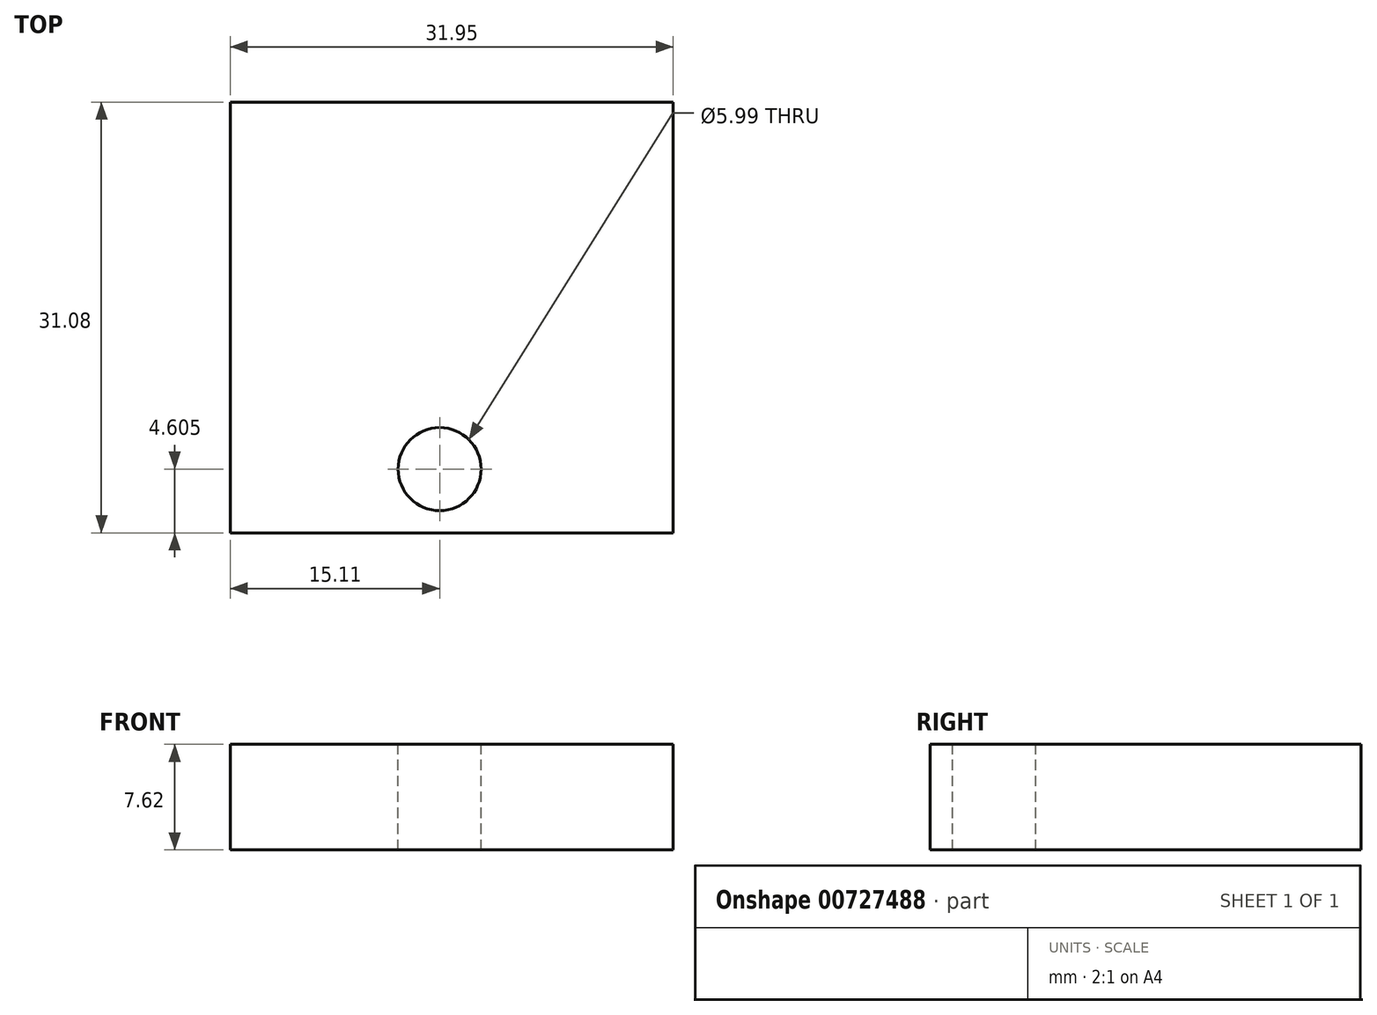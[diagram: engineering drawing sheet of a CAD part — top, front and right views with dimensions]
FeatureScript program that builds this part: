
annotation { "Feature Type Name" : "Feature", "Feature Type Description" : "" }
export const myFeature = defineFeature(function(context is Context, id is Id, definition is map)
    precondition{}
    {
        {
            var Q0;
            Q0=qCreatedBy(makeId("Top.planeOp"),FACE);
            var sketch = newSketch(context, id + "F0", { "sketchPlane" : qUnion([Q0])});
            skLineSegment(sketch, "E0.bottom", {"start": v(-15.1, 10.8) * mm, "end": v(16.84, 10.8) * mm});
            skLineSegment(sketch, "E0.top", {"start": v(-15.1, -20.3) * mm, "end": v(16.84, -20.3) * mm});
            skLineSegment(sketch, "E0.left", {"start": v(-15.1, 10.8) * mm, "end": v(-15.1, -20.3) * mm});
            skLineSegment(sketch, "E0.right", {"start": v(16.84, 10.8) * mm, "end": v(16.84, -20.3) * mm});
            skSolve(sketch);
        }
        {
            var Q0;
            Q0 = qSketchRegion(id + "F0", true);
            extrude(context, id + "F1", {"entities" : qUnion([Q0]), "depth" : 7.62 * mm, "offsetDistance" : 25.4 * mm});
        }
        {
            var Q0;
            Q0=makeQuery(id+"F1.opExtrude","CAP_FACE",FACE,{"disambiguationData":[OSD([sQuery(id+"F0.wireOp",EDGE,"E0.bottom"),sQuery(id+"F0.wireOp",EDGE,"E0.top"),sQuery(id+"F0.wireOp",EDGE,"E0.left"),sQuery(id+"F0.wireOp",EDGE,"E0.right")])],"isStart":false});
            var sketch = newSketch(context, id + "F2", { "sketchPlane" : qUnion([Q0])});
            skSolve(sketch);
        }
        {
            var Q0;
            Q0=makeQuery(id+"F2.imprint","IMPRINT",FACE,{"disambiguationData":[TD([[makeQuery(id+"F2.imprint","IMPRINT",EDGE,{"derivedFrom":makeQuery(id+"F1.opExtrude","CAP_EDGE",EDGE,{"disambiguationData":[OSD([sQuery(id+"F0.wireOp",EDGE,"E0.bottom")])],"isStart":false})}),-1.0]])]});
            var sketch = newSketch(context, id + "F3", { "sketchPlane" : qUnion([Q0])});
            skCircle(sketch, "E1", {"center": v(0, -15.69) * mm, "radius": 3 * mm});
            skSolve(sketch);
        }
        {
            var Q0;
            Q0 = qSketchRegion(id + "F3", true);
            extrude(context, id + "F4", {"entities" : qUnion([Q0]), "operationType" : NewBodyOperationType.REMOVE, "oppositeDirection" : true, "depth" : 25.4 * mm, "offsetDistance" : 25.4 * mm});
        }
    });
